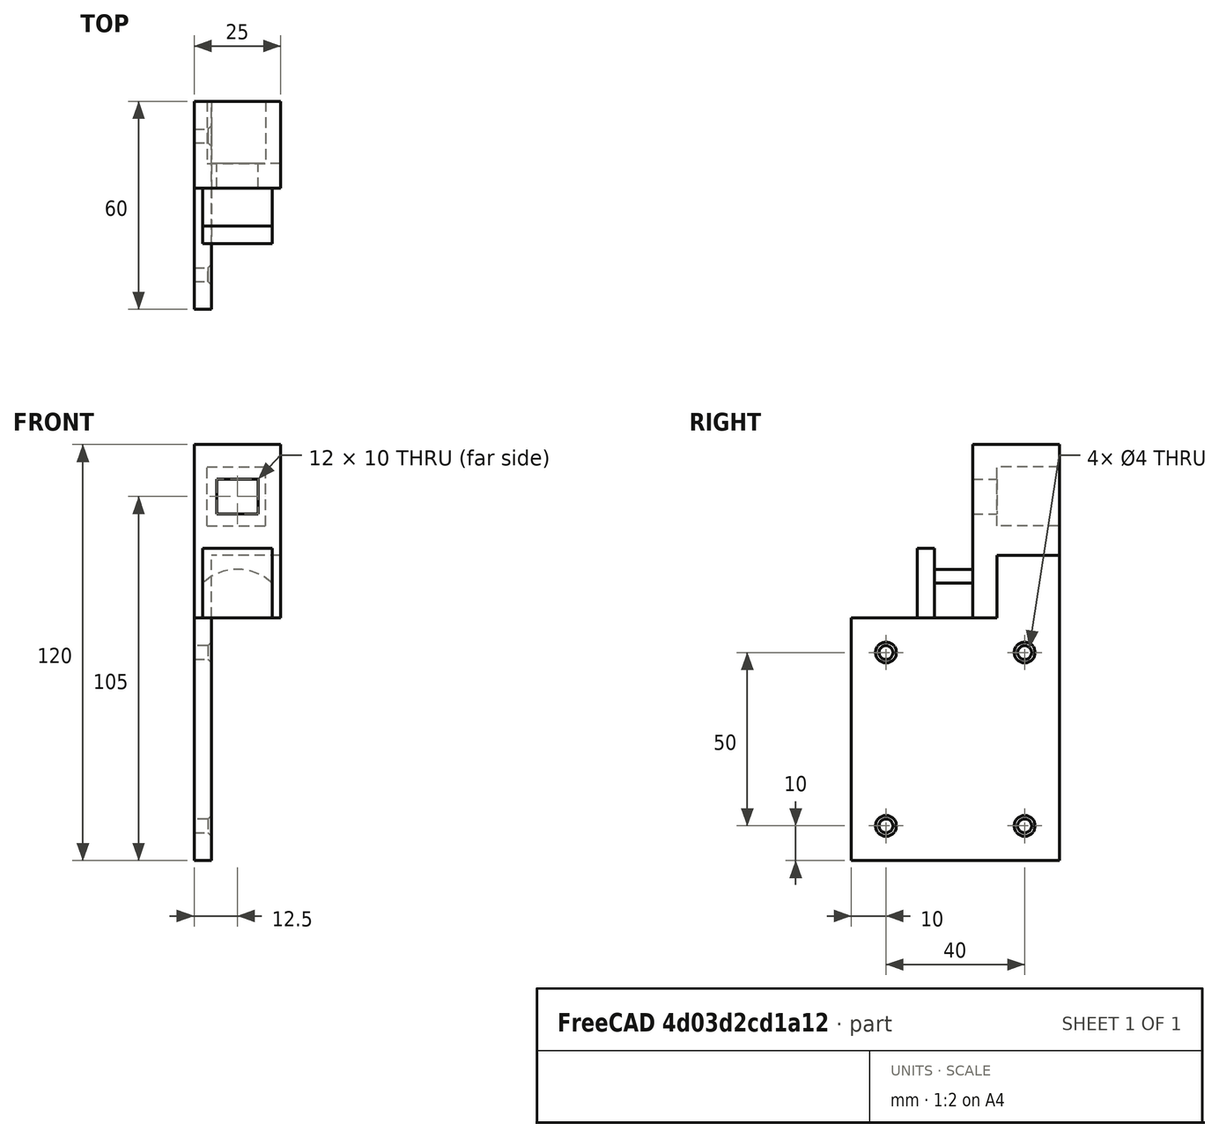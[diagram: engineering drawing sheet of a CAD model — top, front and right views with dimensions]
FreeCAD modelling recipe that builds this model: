
FCSTD DOCUMENT  (FreeCAD 0.20R29603 (Git))
Label: window_fixation
License: All rights reserved
LicenseURL: http://en.wikipedia.org/wiki/All_rights_reserved
objects: TechDraw::DrawViewDimension×17, Sketcher::SketchObject×8, PartDesign::Pad×4, PartDesign::Pocket×4, TechDraw::DrawProjGroupItem×3, PartDesign::Chamfer×1, PartDesign::Body×1, TechDraw::DrawSVGTemplate×1, TechDraw::DrawProjGroup×1, TechDraw::DrawPage×1
note: 27 computed .brp shape members not serialized (recipe doc carries the construction recipe); baked Part::Feature solids carry a one-line shape summary decoded from their .brp

FEATURE [Sketcher::SketchObject] Sketch
  FullyConstrained = false
  MapMode = 5
  Placement = pos=(0,0,0) rot=(1,0,0;1.5708rad)
  Support = -> [XZ_Plane001]
  sketch-geometry (4):
    g0: LineSegment StartX=7.5 StartY=0 StartZ=0 EndX=32.5 EndY=0 EndZ=0
    g1: LineSegment StartX=7.5 StartY=0 StartZ=0 EndX=7.5 EndY=50 EndZ=0
    g2: LineSegment StartX=7.5 StartY=50 StartZ=0 EndX=32.5 EndY=50 EndZ=0
    g3: LineSegment StartX=32.5 StartY=50 StartZ=0 EndX=32.5 EndY=0 EndZ=0
  constraints (11):
    c: Horizontal(g0)
    c: Distance(g0) = 25
    c: Coincident(g1,g0)
    c: Vertical(g1)
    c: Distance(g1) = 50
    c: Coincident(g2,g1)
    c: Horizontal(g2)
    c: Coincident(g3,g2)
    c: Coincident(g3,g0)
    c: Vertical(g3)
    c: DistanceX(g-1,g0) = 7.5
FEATURE [PartDesign::Pad] Pad
  Direction = (0,-1,2e-16)
  Length = 25
  Length2 = 10
  Placement = pos=(0,0,0) rot=(1,0,0;1.5708rad)
  Profile = -> Sketch
  Type = 0
FEATURE [Sketcher::SketchObject] Sketch001
  FullyConstrained = true
  MapMode = 5
  Placement = pos=(0,-25,1e-16) rot=(1,0,0;1.5708rad)
  Support = -> [Pad]
  sketch-geometry (4):
    g0: LineSegment StartX=14 StartY=30 StartZ=0 EndX=26 EndY=30 EndZ=0
    g1: LineSegment StartX=14 StartY=30 StartZ=0 EndX=14 EndY=40 EndZ=0
    g2: LineSegment StartX=14 StartY=40 StartZ=0 EndX=26 EndY=40 EndZ=0
    g3: LineSegment StartX=26 StartY=30 StartZ=0 EndX=26 EndY=40 EndZ=0
  constraints (12):
    c: Horizontal(g0)
    c: DistanceY(g-1,g0) = 30
    c: Coincident(g1,g0)
    c: Vertical(g1)
    c: Distance(g1) = 10
    c: Distance(g0) = 12
    c: Coincident(g2,g1)
    c: Horizontal(g2)
    c: Coincident(g3,g0)
    c: Coincident(g3,g2)
    c: Equal(g0,g2)
    c: DistanceX(g-1,g0) = 14
FEATURE [Sketcher::SketchObject] Sketch002
  FullyConstrained = true
  MapMode = 5
  Placement = pos=(0,0,0) rot=(-1,0,0;1.5708rad)
  sketch-geometry (4):
    g0: LineSegment StartX=11.1929 StartY=-26.5 StartZ=0 EndX=28.1929 EndY=-26.5 EndZ=0
    g1: LineSegment StartX=11.1929 StartY=-26.5 StartZ=0 EndX=11.1929 EndY=-43.5 EndZ=0
    g2: LineSegment StartX=11.1929 StartY=-43.5 StartZ=0 EndX=28.1929 EndY=-43.5 EndZ=0
    g3: LineSegment StartX=28.1929 StartY=-26.5 StartZ=0 EndX=28.1929 EndY=-43.5 EndZ=0
  constraints (12):
    c: Horizontal(g0)
    c: Distance(g0) = 17
    c: DistanceY(g0,g-1) = 26.5
    c: Coincident(g1,g0)
    c: Vertical(g1)
    c: Distance(g1) = 17
    c: Coincident(g2,g1)
    c: Horizontal(g2)
    c: Coincident(g3,g0)
    c: Coincident(g3,g2)
    c: Vertical(g3)
    c: Equal(g0,g2)
FEATURE [PartDesign::Pocket] Pocket
  BaseFeature = -> Pad
  Direction = (1,1,1)
  Length = 5
  Length2 = 5
  Placement = pos=(0,0,0) rot=(1,0,0;1.5708rad)
  Profile = -> Sketch001
  Type = 1
FEATURE [PartDesign::Pocket] Pocket001
  BaseFeature = -> Pocket
  Direction = (1,1,1)
  Length = 18
  Length2 = 5
  Placement = pos=(0,0,0) rot=(1,0,0;1.5708rad)
  Profile = -> Sketch002
  Type = 0
FEATURE [Sketcher::SketchObject] Sketch003
  FullyConstrained = false
  MapMode = 5
  Placement = pos=(0,-25,1e-16) rot=(1,0,0;1.5708rad)
  Support = -> [Pocket001]
  sketch-geometry (5):
    g0: LineSegment StartX=10 StartY=0 StartZ=0 EndX=30 EndY=0 EndZ=0
    g1: LineSegment StartX=10 StartY=0 StartZ=0 EndX=10 EndY=10 EndZ=0
    g2: LineSegment StartX=30 StartY=0 StartZ=0 EndX=30 EndY=10 EndZ=0
    g3: ArcOfCircle CenterX=20 CenterY=-0.499997 CenterZ=0 NormalX=0 NormalY=0 NormalZ=1 AngleXU=0 Radius=14.5 StartAngle=0.809783 EndAngle=2.33181
    g4: GeomPoint X=19.9952 Y=14 Z=0
  constraints (14):
    c: PointOnObject(g0,g-1)
    c: PointOnObject(g0,g-1)
    c: Distance(g0) = 20
    c: DistanceX(g-1,g0) = 10
    c: Coincident(g1,g0)
    c: Vertical(g1)
    c: Distance(g1) = 10
    c: Coincident(g2,g0)
    c: Vertical(g2)
    c: Equal(g1,g2)
    c: Coincident(g3,g1)
    c: Coincident(g3,g2)
    c: PointOnObject(g4,g3)
    c: DistanceY(g-1,g4) = 14
FEATURE [PartDesign::Pad] Pad001
  BaseFeature = -> Pocket001
  Direction = (0,-1,0)
  Length = 11
  Length2 = 10
  Placement = pos=(0,0,0) rot=(1,0,0;1.5708rad)
  Profile = -> Sketch003
  Type = 0
FEATURE [Sketcher::SketchObject] Sketch005
  FullyConstrained = true
  MapMode = 5
  Placement = pos=(0,-36,-1e-14) rot=(1,0,0;1.5708rad)
  sketch-geometry (4):
    g0: LineSegment StartX=10 StartY=0 StartZ=0 EndX=30 EndY=0 EndZ=0
    g1: LineSegment StartX=10 StartY=0 StartZ=0 EndX=10 EndY=20 EndZ=0
    g2: LineSegment StartX=10 StartY=20 StartZ=0 EndX=30 EndY=20 EndZ=0
    g3: LineSegment StartX=30 StartY=20 StartZ=0 EndX=30 EndY=0 EndZ=0
  constraints (12):
    c: PointOnObject(g0,g-1)
    c: PointOnObject(g0,g-1)
    c: Distance(g0) = 20
    c: DistanceX(g-1,g0) = 10
    c: Coincident(g1,g0)
    c: Vertical(g1)
    c: Distance(g1) = 20
    c: Coincident(g2,g1)
    c: Horizontal(g2)
    c: Coincident(g3,g2)
    c: Coincident(g3,g0)
    c: Equal(g1,g3)
FEATURE [PartDesign::Pad] Pad003
  BaseFeature = -> Pad001
  Direction = (0,-1,4e-16)
  Length = 5
  Length2 = 10
  Placement = pos=(0,0,0) rot=(1,0,0;1.5708rad)
  Profile = -> Sketch005
  Type = 0
FEATURE [Sketcher::SketchObject] Sketch006
  FullyConstrained = true
  MapMode = 5
  Placement = pos=(7.5,0,0) rot=(0.707107,0,-0.707107;3.14159rad)
  Support = -> [Pad003]
  sketch-geometry (4):
    g0: LineSegment StartX=0 StartY=0 StartZ=0 EndX=0 EndY=60 EndZ=0
    g1: LineSegment StartX=0 StartY=0 StartZ=0 EndX=70 EndY=0 EndZ=0
    g2: LineSegment StartX=0 StartY=60 StartZ=0 EndX=70 EndY=60 EndZ=0
    g3: LineSegment StartX=70 StartY=60 StartZ=0 EndX=70 EndY=0 EndZ=0
  constraints (11):
    c: Coincident(g0,g-1)
    c: PointOnObject(g0,g-2)
    c: Distance(g0) = 60
    c: Coincident(g1,g0)
    c: Horizontal(g1)
    c: Distance(g1) = 70
    c: Coincident(g2,g0)
    c: Horizontal(g2)
    c: Equal(g2,g1)
    c: Coincident(g3,g2)
    c: Coincident(g3,g1)
FEATURE [PartDesign::Pad] Pad004
  BaseFeature = -> Pad003
  Direction = (1,0,0)
  Length = 5
  Length2 = 100
  Placement = pos=(0,0,0) rot=(1,0,0;1.5708rad)
  Profile = -> Sketch006
  Type = 0
  UseCustomVector = true
FEATURE [Sketcher::SketchObject] Sketch007
  FullyConstrained = true
  MapMode = 5
  Placement = pos=(32.5,0,0) rot=(0.707107,0,0.707107;3.14159rad)
  Support = -> [Pad004]
  sketch-geometry (4):
    g0: LineSegment StartX=0 StartY=0 StartZ=0 EndX=18 EndY=0 EndZ=0
    g1: LineSegment StartX=18 StartY=0 StartZ=0 EndX=18 EndY=18 EndZ=0
    g2: LineSegment StartX=18 StartY=18 StartZ=0 EndX=0 EndY=18 EndZ=0
    g3: LineSegment StartX=0 StartY=18 StartZ=0 EndX=0 EndY=0 EndZ=0
  constraints (11):
    c: Coincident(g0,g-1)
    c: PointOnObject(g0,g-1)
    c: Distance(g0) = 18
    c: Coincident(g1,g0)
    c: Vertical(g1)
    c: Distance(g1) = 18
    c: Coincident(g2,g1)
    c: Horizontal(g2)
    c: Equal(g2,g0)
    c: Coincident(g3,g2)
    c: Coincident(g3,g0)
FEATURE [PartDesign::Pocket] Pocket002
  BaseFeature = -> Pad004
  Direction = (1,1,1)
  Length = 20
  Length2 = 100
  Placement = pos=(0,0,0) rot=(1,0,0;1.5708rad)
  Profile = -> Sketch007
  Type = 0
FEATURE [Sketcher::SketchObject] Sketch008
  ExternalGeometry = -> [Pocket002]
  FullyConstrained = true
  MapMode = 5
  Placement = pos=(12.5,0,2.9e-15) rot=(0.707107,0,0.707107;3.14159rad)
  Support = -> [Pocket002]
  sketch-geometry (13):
    g0: LineSegment StartX=-2.9e-15 StartY=0 StartZ=0 EndX=-2.9e-15 EndY=60 EndZ=0
    g1: Circle CenterX=-60 CenterY=50 CenterZ=0 NormalX=0 NormalY=0 NormalZ=1 AngleXU=0 Radius=2
    g2: Circle CenterX=-10 CenterY=50 CenterZ=0 NormalX=0 NormalY=0 NormalZ=1 AngleXU=0 Radius=2
    g3: Circle CenterX=-60 CenterY=10 CenterZ=0 NormalX=0 NormalY=0 NormalZ=1 AngleXU=0 Radius=2
    g4: Circle CenterX=-10 CenterY=10 CenterZ=0 NormalX=0 NormalY=0 NormalZ=1 AngleXU=0 Radius=2
    g5: LineSegment StartX=-60 StartY=50 StartZ=0 EndX=-60 EndY=60 EndZ=0
    g6: LineSegment StartX=-60 StartY=50 StartZ=0 EndX=-70 EndY=50 EndZ=0
    g7: LineSegment StartX=-10 StartY=50 StartZ=0 EndX=-10 EndY=60 EndZ=0
    g8: LineSegment StartX=-10 StartY=50 StartZ=0 EndX=-3.6e-15 EndY=50 EndZ=0
    g9: LineSegment StartX=-10 StartY=10 StartZ=0 EndX=-3.6e-15 EndY=10 EndZ=0
    g10: LineSegment StartX=-10 StartY=10 StartZ=0 EndX=-10 EndY=0 EndZ=0
    g11: LineSegment StartX=-60 StartY=10 StartZ=0 EndX=-70 EndY=10 EndZ=0
    g12: LineSegment StartX=-60 StartY=10 StartZ=0 EndX=-60 EndY=0 EndZ=0
  constraints (38):
    c: Coincident(g0,g-5)
    c: Coincident(g0,g-3)
    c: Diameter(g1) = 4
    c: Diameter(g2) = 4
    c: Diameter(g4) = 4
    c: Diameter(g3) = 4
    c: Coincident(g5,g1)
    c: PointOnObject(g5,g-3)
    c: Coincident(g6,g1)
    c: PointOnObject(g6,g-4)
    c: Horizontal(g6)
    c: Vertical(g5)
    c: Coincident(g7,g2)
    c: PointOnObject(g7,g-3)
    c: Vertical(g7)
    c: Coincident(g8,g2)
    c: PointOnObject(g8,g0)
    c: Horizontal(g8)
    c: Coincident(g9,g4)
    c: PointOnObject(g9,g0)
    c: Horizontal(g9)
    c: Coincident(g10,g4)
    c: PointOnObject(g10,g-5)
    c: Vertical(g10)
    c: Coincident(g11,g3)
    c: PointOnObject(g11,g-4)
    c: Horizontal(g11)
    c: Coincident(g12,g3)
    c: PointOnObject(g12,g-5)
    c: Vertical(g12)
    c: Equal(g5,g7)
    c: Equal(g12,g10)
    c: Equal(g11,g9)
    c: Equal(g6,g8)
    c: Equal(g12,g5)
    c: Equal(g11,g6)
    c: Distance(g5) = 10
    c: Distance(g6) = 10
FEATURE [PartDesign::Pocket] Pocket003
  BaseFeature = -> Pocket002
  Direction = (-1,0,-2e-16)
  Length = 5
  Length2 = 5
  Placement = pos=(0,0,0) rot=(1,0,0;1.5708rad)
  Profile = -> Sketch008
  ReferenceAxis = -> Sketch008 [N_Axis]
  Type = 1
FEATURE [PartDesign::Chamfer] Chamfer
  Angle = 45
  Base = -> Pocket003 [Edge35,Edge33,Edge34,Edge32]
  BaseFeature = -> Pocket003
  ChamferType = 0
  FlipDirection = false
  Placement = pos=(0,0,0) rot=(1,0,0;1.5708rad)
  Size = 1
  Size2 = 1
  SupportTransform = false
  UseAllEdges = false
FEATURE [PartDesign::Body] Body
  Group = -> [Sketch,Pad,Sketch001,Sketch002,Pocket,Pocket001,Sketch003,Pad001,Sketch005,Pad003,Sketch006,Pad004,Sketch007,Pocket002,Sketch008,Pocket003,Chamfer]
  Origin = -> Origin001
  Tip = -> Chamfer
FEATURE [TechDraw::DrawSVGTemplate] Template
  EditableTexts = Designed_by_Name=Белкин Никита; FC-Date=20.04.2023; FC-SC=1:1; FC-Title=Крепление к створке
  Height = 210
  Orientation = 1
  Width = 297
FEATURE [TechDraw::DrawProjGroupItem] ProjItem  label="Front"
  CoarseView = false
  Direction = (1,0,0)
  Focus = 100
  HardHidden = false
  IsoCount = 0
  IsoHidden = false
  IsoVisible = false
  LockPosition = true
  Perspective = false
  Rotation = 0
  RotationVector = (0,1,0)
  ScaleType = 2
  SeamHidden = false
  SeamVisible = true
  SmoothHidden = false
  SmoothVisible = true
  Source = -> [Body]
  Type = 0
  X = 0
  XDirection = (0,1,0)
  Y = 0
FEATURE [TechDraw::DrawProjGroupItem] ProjItem001  label="Top"
  CoarseView = false
  Direction = (0,0,1)
  Focus = 100
  HardHidden = false
  IsoCount = 0
  IsoHidden = false
  IsoVisible = false
  LockPosition = false
  Perspective = false
  Rotation = 0
  RotationVector = (1,0,0)
  ScaleType = 2
  SeamHidden = false
  SeamVisible = true
  SmoothHidden = false
  SmoothVisible = true
  Source = -> [Body]
  Type = 4
  X = 0
  XDirection = (0,1,0)
  Y = -88.1307
FEATURE [TechDraw::DrawProjGroupItem] ProjItem002  label="Left"
  CoarseView = false
  Direction = (1e-16,-1,0)
  Focus = 100
  HardHidden = false
  IsoCount = 0
  IsoHidden = false
  IsoVisible = false
  LockPosition = false
  Perspective = false
  Rotation = 0
  RotationVector = (1,0,0)
  ScaleType = 2
  SeamHidden = false
  SeamVisible = true
  SmoothHidden = false
  SmoothVisible = true
  Source = -> [Body]
  Type = 1
  X = 75
  XDirection = (1,1e-16,0)
  Y = 0
FEATURE [TechDraw::DrawProjGroup] ProjGroup
  Anchor = -> ProjItem
  AutoDistribute = true
  LockPosition = false
  ProjectionType = 0
  Rotation = 0
  ScaleType = 0
  Source = -> [Body]
  Views = -> [ProjItem,ProjItem001,ProjItem002]
  X = 82.168
  Y = 134.79
  spacingX = 15
  spacingY = 15
FEATURE [TechDraw::DrawViewDimension] Dimension
  AngleOverride = false
  Arbitrary = false
  ArbitraryTolerances = false
  EqualTolerance = true
  ExtensionAngle = 0
  FormatSpec = %.2w
  FormatSpecOverTolerance = %+.2w
  FormatSpecUnderTolerance = %+.2w
  Inverted = false
  LineAngle = 0
  LockPosition = false
  MeasureType = 1
  OverTolerance = 0
  References2D = -> [ProjItem]
  Rotation = 0
  ScaleType = 0
  TheoreticalExact = false
  Type = 1
  UnderTolerance = 0
  X = -1.37916
  Y = -61.1778
FEATURE [TechDraw::DrawViewDimension] Dimension001
  AngleOverride = false
  Arbitrary = false
  ArbitraryTolerances = false
  EqualTolerance = true
  ExtensionAngle = 0
  FormatSpec = %.2w
  FormatSpecOverTolerance = %+.2w
  FormatSpecUnderTolerance = %+.2w
  Inverted = false
  LineAngle = 0
  LockPosition = false
  MeasureType = 1
  OverTolerance = 0
  References2D = -> [ProjItem]
  Rotation = 0
  ScaleType = 0
  TheoreticalExact = false
  Type = 2
  UnderTolerance = 0
  X = -36.8958
  Y = -21.3967
FEATURE [TechDraw::DrawViewDimension] Dimension002
  AngleOverride = false
  Arbitrary = false
  ArbitraryTolerances = false
  EqualTolerance = true
  ExtensionAngle = 0
  FormatSpec = %.2w
  FormatSpecOverTolerance = %+.2w
  FormatSpecUnderTolerance = %+.2w
  Inverted = false
  LineAngle = 0
  LockPosition = false
  MeasureType = 1
  OverTolerance = 0
  References2D = -> [ProjItem]
  Rotation = 0
  ScaleType = 0
  TheoreticalExact = false
  Type = 2
  UnderTolerance = 0
  X = 34.4133
  Y = 3.05166
FEATURE [TechDraw::DrawViewDimension] Dimension004
  AngleOverride = false
  Arbitrary = false
  ArbitraryTolerances = false
  EqualTolerance = true
  ExtensionAngle = 0
  FormatSpec = %.2w
  FormatSpecOverTolerance = %+.2w
  FormatSpecUnderTolerance = %+.2w
  Inverted = false
  LineAngle = 0
  LockPosition = false
  MeasureType = 1
  OverTolerance = 0
  References2D = -> [ProjItem]
  Rotation = 0
  ScaleType = 0
  TheoreticalExact = false
  Type = 1
  UnderTolerance = 0
  X = -15.2146
  Y = 39.2146
FEATURE [TechDraw::DrawViewDimension] Dimension006
  AngleOverride = false
  Arbitrary = false
  ArbitraryTolerances = false
  EqualTolerance = true
  ExtensionAngle = 0
  FormatSpec = %.2w
  FormatSpecOverTolerance = %+.2w
  FormatSpecUnderTolerance = %+.2w
  Inverted = false
  LineAngle = 0
  LockPosition = false
  MeasureType = 1
  OverTolerance = 0
  References2D = -> [ProjItem002]
  Rotation = 0
  ScaleType = 0
  TheoreticalExact = false
  Type = 2
  UnderTolerance = 0
  X = -21.1124
  Y = 38.0746
FEATURE [TechDraw::DrawViewDimension] Dimension007
  AngleOverride = false
  Arbitrary = false
  ArbitraryTolerances = false
  EqualTolerance = true
  ExtensionAngle = 0
  FormatSpec = %.2w
  FormatSpecOverTolerance = %+.2w
  FormatSpecUnderTolerance = %+.2w
  Inverted = false
  LineAngle = 0
  LockPosition = false
  MeasureType = 1
  OverTolerance = 0
  References2D = -> [ProjItem002]
  Rotation = 0
  ScaleType = 0
  TheoreticalExact = false
  Type = 1
  UnderTolerance = 0
  X = -19.8129
  Y = -62.2842
FEATURE [TechDraw::DrawViewDimension] Dimension008
  AngleOverride = false
  Arbitrary = false
  ArbitraryTolerances = false
  EqualTolerance = true
  ExtensionAngle = 0
  FormatSpec = %.2w
  FormatSpecOverTolerance = %+.2w
  FormatSpecUnderTolerance = %+.2w
  Inverted = false
  LineAngle = 0
  LockPosition = false
  MeasureType = 1
  OverTolerance = 0
  References2D = -> [ProjItem002]
  Rotation = 0
  ScaleType = 0
  TheoreticalExact = false
  Type = 2
  UnderTolerance = 0
  X = -20.9975
  Y = -21.8104
FEATURE [TechDraw::DrawViewDimension] Dimension009
  AngleOverride = false
  Arbitrary = false
  ArbitraryTolerances = false
  EqualTolerance = true
  ExtensionAngle = 0
  FormatSpec = %.2w
  FormatSpecOverTolerance = %+.2w
  FormatSpecUnderTolerance = %+.2w
  Inverted = false
  LineAngle = 0
  LockPosition = false
  MeasureType = 1
  OverTolerance = 0
  References2D = -> [ProjItem002]
  Rotation = 0
  ScaleType = 0
  TheoreticalExact = false
  Type = 1
  UnderTolerance = 0
  X = -0.125729
  Y = 59.151
FEATURE [TechDraw::DrawViewDimension] Dimension010
  AngleOverride = false
  Arbitrary = false
  ArbitraryTolerances = false
  EqualTolerance = true
  ExtensionAngle = 0
  FormatSpec = %.2w
  FormatSpecOverTolerance = %+.2w
  FormatSpecUnderTolerance = %+.2w
  Inverted = false
  LineAngle = 0
  LockPosition = false
  MeasureType = 1
  OverTolerance = 0
  References2D = -> [ProjItem002]
  Rotation = 0
  ScaleType = 0
  TheoreticalExact = false
  Type = 2
  UnderTolerance = 0
  X = 17.1634
  Y = 59.95
FEATURE [TechDraw::DrawViewDimension] Dimension011
  AngleOverride = false
  Arbitrary = false
  ArbitraryTolerances = false
  EqualTolerance = true
  ExtensionAngle = 0
  FormatSpec = %.2w
  FormatSpecOverTolerance = %+.2w
  FormatSpecUnderTolerance = %+.2w
  Inverted = false
  LineAngle = 0
  LockPosition = false
  MeasureType = 1
  OverTolerance = 0
  References2D = -> [ProjItem002]
  Rotation = 0
  ScaleType = 0
  TheoreticalExact = false
  Type = 2
  UnderTolerance = 0
  X = 22.4197
  Y = 22.5
FEATURE [TechDraw::DrawViewDimension] Dimension012
  AngleOverride = false
  Arbitrary = false
  ArbitraryTolerances = false
  EqualTolerance = true
  ExtensionAngle = 0
  FormatSpec = %.2w
  FormatSpecOverTolerance = %+.2w
  FormatSpecUnderTolerance = %+.2w
  Inverted = false
  LineAngle = 0
  LockPosition = false
  MeasureType = 1
  OverTolerance = 0
  References2D = -> [ProjItem]
  Rotation = 0
  ScaleType = 0
  TheoreticalExact = false
  Type = 2
  UnderTolerance = 0
  X = -25.5144
  Y = 14.8477
FEATURE [TechDraw::DrawViewDimension] Dimension013
  AngleOverride = false
  Arbitrary = false
  ArbitraryTolerances = false
  EqualTolerance = true
  ExtensionAngle = 0
  FormatSpec = %.2w
  FormatSpecOverTolerance = %+.2w
  FormatSpecUnderTolerance = %+.2w
  Inverted = false
  LineAngle = 0
  LockPosition = false
  MeasureType = 1
  OverTolerance = 0
  References2D = -> [ProjItem002]
  Rotation = 0
  ScaleType = 0
  TheoreticalExact = false
  Type = 1
  UnderTolerance = 0
  X = -1.09602
  Y = 7.1235
FEATURE [TechDraw::DrawViewDimension] Dimension014
  AngleOverride = false
  Arbitrary = false
  ArbitraryTolerances = false
  EqualTolerance = true
  ExtensionAngle = 0
  FormatSpec = %.2w
  FormatSpecOverTolerance = %+.2w
  FormatSpecUnderTolerance = %+.2w
  Inverted = false
  LineAngle = 0
  LockPosition = false
  MeasureType = 1
  OverTolerance = 0
  References2D = -> [ProjItem001]
  Rotation = 0
  ScaleType = 0
  TheoreticalExact = false
  Type = 2
  UnderTolerance = 0
  X = 34.8271
  Y = 2.03299
FEATURE [TechDraw::DrawViewDimension] Dimension015
  AngleOverride = false
  Arbitrary = false
  ArbitraryTolerances = false
  EqualTolerance = true
  ExtensionAngle = 0
  FormatSpec = %.2w
  FormatSpecOverTolerance = %+.2w
  FormatSpecUnderTolerance = %+.2w
  Inverted = false
  LineAngle = 0
  LockPosition = false
  MeasureType = 1
  OverTolerance = 0
  References2D = -> [ProjItem001]
  Rotation = 0
  ScaleType = 0
  TheoreticalExact = false
  Type = 1
  UnderTolerance = 0
  X = -0.775832
  Y = -13.5756
FEATURE [TechDraw::DrawViewDimension] Dimension016
  AngleOverride = false
  Arbitrary = false
  ArbitraryTolerances = false
  EqualTolerance = true
  ExtensionAngle = 0
  FormatSpec = ⌀%.2w
  FormatSpecOverTolerance = %+.2w
  FormatSpecUnderTolerance = %+.2w
  Inverted = false
  LineAngle = 0
  LockPosition = false
  MeasureType = 1
  OverTolerance = 0
  References2D = -> [ProjItem]
  Rotation = 0
  ScaleType = 0
  TheoreticalExact = false
  Type = 5
  UnderTolerance = 0
  X = -5.74649
  Y = -43.8649
FEATURE [TechDraw::DrawViewDimension] Dimension017
  AngleOverride = false
  Arbitrary = false
  ArbitraryTolerances = false
  EqualTolerance = true
  ExtensionAngle = 0
  FormatSpec = ⌀%.2w
  FormatSpecOverTolerance = %+.2w
  FormatSpecUnderTolerance = %+.2w
  Inverted = false
  LineAngle = 0
  LockPosition = false
  MeasureType = 1
  OverTolerance = 0
  References2D = -> [ProjItem]
  Rotation = 0
  ScaleType = 0
  TheoreticalExact = false
  Type = 5
  UnderTolerance = 0
  X = -11.3014
  Y = -35.8198
FEATURE [TechDraw::DrawViewDimension] Dimension018
  AngleOverride = false
  Arbitrary = false
  ArbitraryTolerances = false
  EqualTolerance = true
  ExtensionAngle = 0
  FormatSpec = %.2w
  FormatSpecOverTolerance = %+.2w
  FormatSpecUnderTolerance = %+.2w
  Inverted = false
  LineAngle = 0
  LockPosition = false
  MeasureType = 1
  OverTolerance = 0
  References2D = -> [ProjItem001]
  Rotation = 0
  ScaleType = 0
  TheoreticalExact = false
  Type = 1
  UnderTolerance = 0
  X = -21.4065
  Y = 2.43875
FEATURE [TechDraw::DrawPage] Page
  KeepUpdated = true
  NextBalloonIndex = 1
  ProjectionType = 0
  Template = -> Template
  Views = -> [ProjGroup,Dimension,Dimension001,Dimension002,Dimension004,Dimension006,Dimension007,Dimension008,Dimension009,Dimension010,Dimension011,Dimension012,Dimension013,Dimension014,Dimension015,Dimension016,Dimension017,Dimension018]
